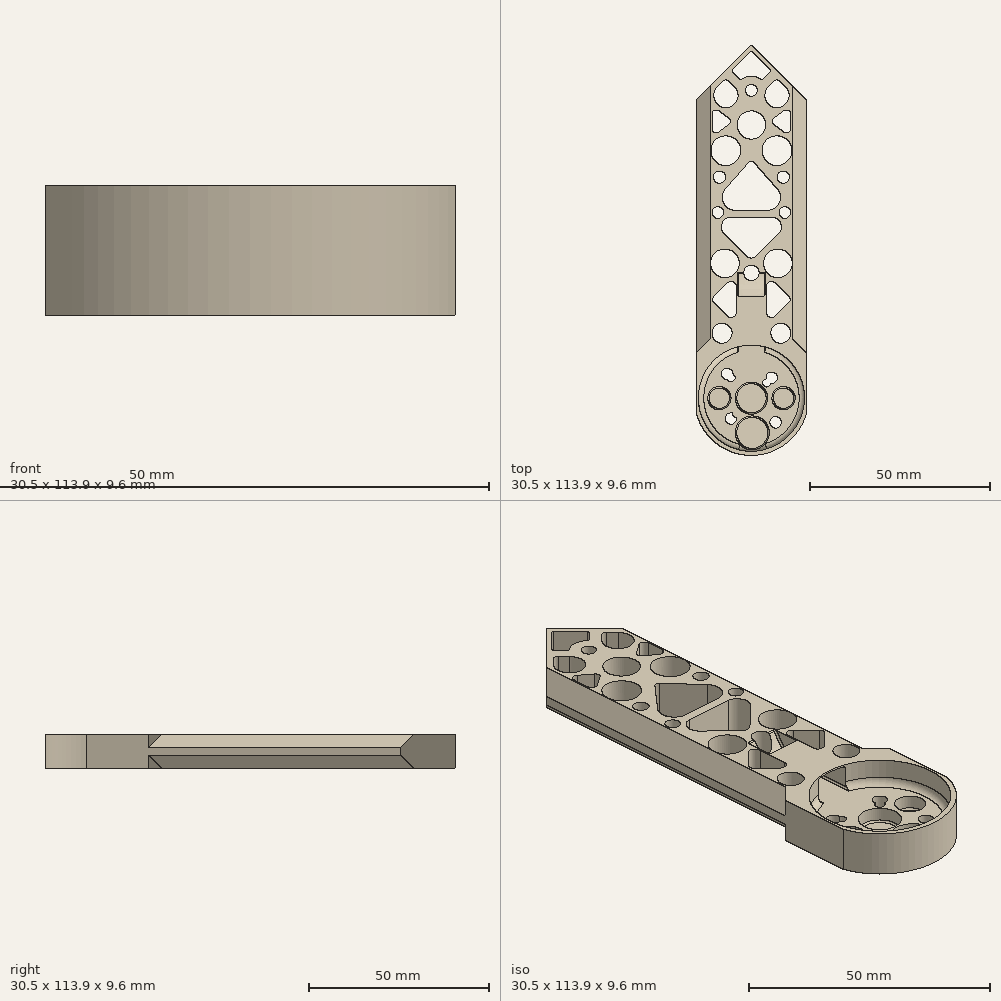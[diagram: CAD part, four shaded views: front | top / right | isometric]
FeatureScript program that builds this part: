
annotation { "Feature Type Name" : "Feature", "Feature Type Description" : "" }
export const myFeature = defineFeature(function(context is Context, id is Id, definition is map)
    precondition{}
    {
        {
            var Q0;
            Q0=qCreatedBy(makeId("Top.planeOp"),FACE);
            var sketch = newSketch(context, id + "F0", { "sketchPlane" : qUnion([Q0])});
            skLineSegment(sketch, "E0", {"start": v(0, 0) * mm, "end": v(-10, 0) * mm});
            skLineSegment(sketch, "E1", {"start": v(-7.84, 7.84) * mm, "end": v(0, 0) * mm});
            skLineSegment(sketch, "E2", {"start": v(-6.78, -6.78) * mm, "end": v(0, 0) * mm});
            skLineSegment(sketch, "E3", {"start": v(0, 0) * mm, "end": v(-5.66, -5.66) * mm});
            skCircle(sketch, "E4", {"center": v(-5.66, -5.66) * mm, "radius": 1.59 * mm});
            skLineSegment(sketch, "E5", {"start": v(0, 0) * mm, "end": v(-6.72, 6.72) * mm});
            skCircle(sketch, "E6", {"center": v(-6.72, 6.72) * mm, "radius": 1.59 * mm});
            skLineSegment(sketch, "E7", {"start": v(0, 0) * mm, "end": v(-5.66, 5.66) * mm});
            skCircle(sketch, "E8", {"center": v(-5.66, 5.66) * mm, "radius": 1.13 * mm});
            skLineSegment(sketch, "E9.MirrorCS", {"start": v(7.84, -7.84) * mm, "end": v(0, 0) * mm});
            skLineSegment(sketch, "E10.MirrorCS", {"start": v(0, 0) * mm, "end": v(5.66, -5.66) * mm});
            skCircle(sketch, "E11.MirrorC", {"center": v(6.72, -6.72) * mm, "radius": 1.59 * mm});
            skCircle(sketch, "E12.MirrorC", {"center": v(5.66, -5.66) * mm, "radius": 1.13 * mm});
            skLineSegment(sketch, "E13.MirrorCS", {"start": v(0, 0) * mm, "end": v(6.72, -6.72) * mm});
            skCircle(sketch, "E14.MirrorC", {"center": v(5.66, 5.66) * mm, "radius": 1.59 * mm});
            skLineSegment(sketch, "E15.MirrorCS", {"start": v(0, 0) * mm, "end": v(5.66, 5.66) * mm});
            skLineSegment(sketch, "E16.MirrorCS", {"start": v(6.78, 6.78) * mm, "end": v(0, 0) * mm});
            skPoint(sketch, "E17.MirrorCS.start.orphan", {"position": v(0, 10) * mm});
            skPoint(sketch, "E18.orphan", {"position": v(10, 10) * mm});
            skPoint(sketch, "E19.orphan", {"position": v(10, -10) * mm});
            skPoint(sketch, "E20.orphan", {"position": v(-10, 10) * mm});
            skPoint(sketch, "E21.orphan", {"position": v(-10, -10) * mm});
            skCircle(sketch, "E22", {"center": v(-4.24, -4.24) * mm, "radius": 1.13 * mm});
            skCircle(sketch, "E23", {"center": v(4.24, 4.24) * mm, "radius": 1.13 * mm});
            skSolve(sketch);
        }
        {
            var Q0;
            Q0=qCreatedBy(makeId("Front.planeOp"),FACE);
            var sketch = newSketch(context, id + "F1", { "sketchPlane" : qUnion([Q0])});
            skLineSegment(sketch, "E24", {"start": v(0, 0) * mm, "end": v(11.35, 0) * mm});
            skLineSegment(sketch, "E25", {"start": v(-11.35, 0) * mm, "end": v(0, 0) * mm});
            skLineSegment(sketch, "E26", {"start": v(0, 0) * mm, "end": v(0, 3.8) * mm});
            skLineSegment(sketch, "E27", {"start": v(0, 3.8) * mm, "end": v(15.25, 3.8) * mm});
            skLineSegment(sketch, "E28", {"start": v(-15.25, 3.8) * mm, "end": v(0, 3.8) * mm});
            skPoint(sketch, "E29.orphan", {"position": v(15.25, 0) * mm});
            skPoint(sketch, "E30.orphan", {"position": v(-15.25, 0) * mm});
            skLineSegment(sketch, "E31", {"start": v(-15.25, 3.8) * mm, "end": v(-11.35, 0) * mm});
            skLineSegment(sketch, "E32", {"start": v(15.25, 3.8) * mm, "end": v(11.35, 0) * mm});
            skLineSegment(sketch, "E33", {"start": v(15.25, 3.8) * mm, "end": v(15.25, 5.8) * mm});
            skLineSegment(sketch, "E34", {"start": v(15.25, 5.8) * mm, "end": v(11.35, 9.6) * mm});
            skLineSegment(sketch, "E35", {"start": v(11.35, 9.6) * mm, "end": v(0, 9.6) * mm});
            skLineSegment(sketch, "E36.MirrorCS", {"start": v(-11.35, 9.6) * mm, "end": v(0, 9.6) * mm});
            skLineSegment(sketch, "E37.MirrorCS", {"start": v(-15.25, 5.8) * mm, "end": v(-11.35, 9.6) * mm});
            skLineSegment(sketch, "E38.MirrorCS", {"start": v(-15.25, 3.8) * mm, "end": v(-15.25, 5.8) * mm});
            skSolve(sketch);
        }
        {
            var Q0;
            Q0=qSketchRegion(id+"F1",true);
            extrude(context, id + "F2", {"entities" : qUnion([Q0]), "depth" : 16.3 * mm, "hasSecondDirection" : true, "secondDirectionOppositeDirection" : true, "secondDirectionDepth" : 98 * mm});
        }
        {
            var Q0;
            Q0=qCreatedBy(makeId("Top.planeOp"),FACE);
            cPlane(context, id + "F3", {"entities" : qUnion([Q0]), "cplaneType" : CPlaneType.OFFSET, "offset" : 16 * mm, "width" : 150 * mm, "height" : 150 * mm});
        }
        {
            var Q0;
            Q0=makeQuery(id+"F2.opExtrude","SWEPT_FACE",FACE,{"disambiguationData":[OSD([sQuery(id+"F1.wireOp",EDGE,"E35"),sQuery(id+"F1.wireOp",EDGE,"E36.MirrorCS")])]});
            var sketch = newSketch(context, id + "F4", { "sketchPlane" : qUnion([Q0])});
            skCircle(sketch, "E39", {"center": v(0, 0) * mm, "radius": 14.75 * mm});
            skLineSegment(sketch, "E40", {"start": v(14.75, 0) * mm, "end": v(-14.75, 0) * mm});
            skSolve(sketch);
        }
        {
            var Q0;
            {var subQ0=sQuery(id+"F4.wireOp",EDGE,"E39");var subQ1=makeQuery(id+"F2.opExtrude","SWEPT_EDGE",EDGE,{"disambiguationData":[OSD([sQuery(id+"F1.wireOp",EDGE,"E34"),sQuery(id+"F1.wireOp",EDGE,"E35")])]});var subQ2=makeQuery(id+"F4.imprint","INTERSECT",VERTEX,{"disambiguationData":[OD(0.0)],"derivedFrom":[subQ1,subQ0]});Q0=makeQuery(id+"F4.imprint","IMPRINT",FACE,{"disambiguationData":[TD([[makeQuery(id+"F4.imprint","IMPRINT",EDGE,{"disambiguationData":[TD([[subQ2,-1.0]])],"derivedFrom":subQ0}),1.0]])]});}
            var Q1;
            {var subQ0=sQuery(id+"F4.wireOp",EDGE,"E39");var subQ1=makeQuery(id+"F2.opExtrude","SWEPT_EDGE",EDGE,{"disambiguationData":[OSD([sQuery(id+"F1.wireOp",EDGE,"E36.MirrorCS"),sQuery(id+"F1.wireOp",EDGE,"E37.MirrorCS")])]});var subQ2=makeQuery(id+"F4.imprint","INTERSECT",VERTEX,{"disambiguationData":[OD(1.0)],"derivedFrom":[subQ1,subQ0]});Q1=makeQuery(id+"F4.imprint","IMPRINT",FACE,{"disambiguationData":[TD([[makeQuery(id+"F4.imprint","IMPRINT",EDGE,{"disambiguationData":[TD([[subQ2,-1.0]])],"derivedFrom":subQ0}),1.0]])]});}
            var Q2;
            {var subQ0=sQuery(id+"F4.wireOp",EDGE,"E40");var subQ1=sQuery(id+"F4.wireOp",EDGE,"E39");var subQ2=makeQuery(id+"F4.imprint","INTERSECT",VERTEX,{"disambiguationData":[OD(1.0)],"derivedFrom":[subQ1,subQ0]});Q2=makeQuery(id+"F4.imprint","IMPRINT",FACE,{"disambiguationData":[TD([[makeQuery(id+"F4.imprint","IMPRINT",EDGE,{"disambiguationData":[TD([[subQ2,-1.0]])],"derivedFrom":subQ1}),1.0]])]});}
            var Q3;
            {var subQ0=sQuery(id+"F4.wireOp",EDGE,"E40");var subQ1=sQuery(id+"F4.wireOp",EDGE,"E39");var subQ2=makeQuery(id+"F4.imprint","INTERSECT",VERTEX,{"disambiguationData":[OD(1.0)],"derivedFrom":[subQ1,subQ0]});Q3=makeQuery(id+"F4.imprint","IMPRINT",FACE,{"disambiguationData":[TD([[makeQuery(id+"F4.imprint","IMPRINT",EDGE,{"disambiguationData":[TD([[subQ2,1.0]])],"derivedFrom":subQ1}),1.0]])]});}
            var Q4;
            {var subQ0=sQuery(id+"F4.wireOp",EDGE,"E40");var subQ1=sQuery(id+"F4.wireOp",EDGE,"E39");var subQ2=makeQuery(id+"F4.imprint","INTERSECT",VERTEX,{"disambiguationData":[OD(0.0)],"derivedFrom":[subQ1,subQ0]});Q4=makeQuery(id+"F4.imprint","IMPRINT",FACE,{"disambiguationData":[TD([[makeQuery(id+"F4.imprint","IMPRINT",EDGE,{"disambiguationData":[TD([[subQ2,-1.0]])],"derivedFrom":subQ1}),1.0]])]});}
            var Q5;
            {var subQ0=sQuery(id+"F4.wireOp",EDGE,"E40");var subQ1=sQuery(id+"F4.wireOp",EDGE,"E39");var subQ2=makeQuery(id+"F4.imprint","INTERSECT",VERTEX,{"disambiguationData":[OD(0.0)],"derivedFrom":[subQ1,subQ0]});Q5=makeQuery(id+"F4.imprint","IMPRINT",FACE,{"disambiguationData":[TD([[makeQuery(id+"F4.imprint","IMPRINT",EDGE,{"disambiguationData":[TD([[subQ2,1.0]])],"derivedFrom":subQ1}),1.0]])]});}
            extrude(context, id + "F5", {"entities" : qUnion([Q0, Q1, Q2, Q3, Q4, Q5]), "operationType" : NewBodyOperationType.REMOVE, "oppositeDirection" : true, "depth" : 5.6 * mm});
        }
        {
            var Q0;
            {var subQ5=sQuery(id+"F0.wireOp",EDGE,"E1");Q0=makeQuery(id+"F0.imprint","IMPRINT",FACE,{"disambiguationData":[TD([[makeQuery(id+"F0.imprint","IMPRINT",EDGE,{"derivedFrom":subQ5}),-1.0]])]});}
            var Q1;
            {var subQ3=sQuery(id+"F0.wireOp",EDGE,"E1");Q1=makeQuery(id+"F0.imprint","IMPRINT",FACE,{"disambiguationData":[TD([[makeQuery(id+"F0.imprint","IMPRINT",EDGE,{"derivedFrom":subQ3}),1.0]])]});}
            var Q2;
            {var subQ5=sQuery(id+"F0.wireOp",EDGE,"E2");Q2=makeQuery(id+"F0.imprint","IMPRINT",FACE,{"disambiguationData":[TD([[makeQuery(id+"F0.imprint","IMPRINT",EDGE,{"derivedFrom":subQ5}),1.0]])]});}
            var Q3;
            {var subQ5=sQuery(id+"F0.wireOp",EDGE,"E2");Q3=makeQuery(id+"F0.imprint","IMPRINT",FACE,{"disambiguationData":[TD([[makeQuery(id+"F0.imprint","IMPRINT",EDGE,{"derivedFrom":subQ5}),-1.0]])]});}
            var Q4;
            {var subQ0=sQuery(id+"F0.wireOp",EDGE,"E22");var subQ3=sQuery(id+"F0.wireOp",EDGE,"E3");var subQ4=makeQuery(id+"F0.imprint","INTERSECT",VERTEX,{"disambiguationData":[OD(0.0)],"derivedFrom":[subQ3,subQ0]});Q4=makeQuery(id+"F0.imprint","IMPRINT",FACE,{"disambiguationData":[TD([[makeQuery(id+"F0.imprint","IMPRINT",EDGE,{"disambiguationData":[TD([[subQ4,-1.0]])],"derivedFrom":subQ3}),1.0]])]});}
            var Q5;
            {var subQ0=sQuery(id+"F0.wireOp",EDGE,"E22");var subQ3=sQuery(id+"F0.wireOp",EDGE,"E3");var subQ4=makeQuery(id+"F0.imprint","INTERSECT",VERTEX,{"disambiguationData":[OD(0.0)],"derivedFrom":[subQ3,subQ0]});Q5=makeQuery(id+"F0.imprint","IMPRINT",FACE,{"disambiguationData":[TD([[makeQuery(id+"F0.imprint","IMPRINT",EDGE,{"disambiguationData":[TD([[subQ4,-1.0]])],"derivedFrom":subQ3}),-1.0]])]});}
            var Q6;
            {var subQ1=sQuery(id+"F0.wireOp",EDGE,"E6");var subQ3=sQuery(id+"F0.wireOp",EDGE,"E8");var subQ5=makeQuery(id+"F0.imprint","INTERSECT",VERTEX,{"disambiguationData":[OD(0.0)],"derivedFrom":[subQ1,subQ3]});Q6=makeQuery(id+"F0.imprint","IMPRINT",FACE,{"disambiguationData":[TD([[makeQuery(id+"F0.imprint","IMPRINT",EDGE,{"disambiguationData":[TD([[subQ5,-1.0]])],"derivedFrom":subQ1}),-1.0]])]});}
            var Q7;
            {var subQ1=sQuery(id+"F0.wireOp",EDGE,"E6");var subQ3=sQuery(id+"F0.wireOp",EDGE,"E8");var subQ5=makeQuery(id+"F0.imprint","INTERSECT",VERTEX,{"disambiguationData":[OD(1.0)],"derivedFrom":[subQ1,subQ3]});Q7=makeQuery(id+"F0.imprint","IMPRINT",FACE,{"disambiguationData":[TD([[makeQuery(id+"F0.imprint","IMPRINT",EDGE,{"disambiguationData":[TD([[subQ5,1.0]])],"derivedFrom":subQ1}),-1.0]])]});}
            var Q8;
            {var subQ3=sQuery(id+"F0.wireOp",EDGE,"E9.MirrorCS");Q8=makeQuery(id+"F0.imprint","IMPRINT",FACE,{"disambiguationData":[TD([[makeQuery(id+"F0.imprint","IMPRINT",EDGE,{"derivedFrom":subQ3}),1.0]])]});}
            var Q9;
            {var subQ3=sQuery(id+"F0.wireOp",EDGE,"E9.MirrorCS");Q9=makeQuery(id+"F0.imprint","IMPRINT",FACE,{"disambiguationData":[TD([[makeQuery(id+"F0.imprint","IMPRINT",EDGE,{"derivedFrom":subQ3}),-1.0]])]});}
            var Q10;
            {var subQ1=sQuery(id+"F0.wireOp",EDGE,"E11.MirrorC");var subQ3=sQuery(id+"F0.wireOp",EDGE,"E12.MirrorC");var subQ5=makeQuery(id+"F0.imprint","INTERSECT",VERTEX,{"disambiguationData":[OD(0.0)],"derivedFrom":[subQ1,subQ3]});Q10=makeQuery(id+"F0.imprint","IMPRINT",FACE,{"disambiguationData":[TD([[makeQuery(id+"F0.imprint","IMPRINT",EDGE,{"disambiguationData":[TD([[subQ5,-1.0]])],"derivedFrom":subQ1}),1.0]])]});}
            var Q11;
            {var subQ1=sQuery(id+"F0.wireOp",EDGE,"E11.MirrorC");var subQ3=sQuery(id+"F0.wireOp",EDGE,"E12.MirrorC");var subQ5=makeQuery(id+"F0.imprint","INTERSECT",VERTEX,{"disambiguationData":[OD(1.0)],"derivedFrom":[subQ1,subQ3]});Q11=makeQuery(id+"F0.imprint","IMPRINT",FACE,{"disambiguationData":[TD([[makeQuery(id+"F0.imprint","IMPRINT",EDGE,{"disambiguationData":[TD([[subQ5,1.0]])],"derivedFrom":subQ1}),1.0]])]});}
            var Q12;
            {var subQ0=sQuery(id+"F0.wireOp",EDGE,"E23");var subQ1=sQuery(id+"F0.wireOp",EDGE,"E14.MirrorC");var subQ2=makeQuery(id+"F0.imprint","INTERSECT",VERTEX,{"disambiguationData":[OD(1.0)],"derivedFrom":[subQ1,subQ0]});Q12=makeQuery(id+"F0.imprint","IMPRINT",FACE,{"disambiguationData":[TD([[makeQuery(id+"F0.imprint","IMPRINT",EDGE,{"disambiguationData":[TD([[subQ2,1.0]])],"derivedFrom":subQ1}),1.0]])]});}
            var Q13;
            {var subQ1=sQuery(id+"F0.wireOp",EDGE,"E16.MirrorCS");var subQ5=makeQuery(id+"F0.imprint","IMPRINT",VERTEX,{"derivedFrom":subQ1});Q13=makeQuery(id+"F0.imprint","IMPRINT",FACE,{"disambiguationData":[TD([[makeQuery(id+"F0.imprint","IMPRINT",EDGE,{"disambiguationData":[TD([[subQ5,1.0]])],"derivedFrom":subQ1}),-1.0]])]});}
            var Q14;
            {var subQ1=sQuery(id+"F0.wireOp",EDGE,"E16.MirrorCS");var subQ5=makeQuery(id+"F0.imprint","IMPRINT",VERTEX,{"derivedFrom":subQ1});Q14=makeQuery(id+"F0.imprint","IMPRINT",FACE,{"disambiguationData":[TD([[makeQuery(id+"F0.imprint","IMPRINT",EDGE,{"disambiguationData":[TD([[subQ5,1.0]])],"derivedFrom":subQ1}),1.0]])]});}
            var Q15;
            {var subQ1=sQuery(id+"F0.wireOp",EDGE,"E3");var subQ3=sQuery(id+"F0.wireOp",EDGE,"E4");var subQ5=makeQuery(id+"F0.imprint","INTERSECT",VERTEX,{"derivedFrom":[subQ1,subQ3]});Q15=makeQuery(id+"F0.imprint","IMPRINT",FACE,{"disambiguationData":[TD([[makeQuery(id+"F0.imprint","IMPRINT",EDGE,{"disambiguationData":[TD([[subQ5,-1.0]])],"derivedFrom":subQ1}),1.0]])]});}
            var Q16;
            {var subQ1=sQuery(id+"F0.wireOp",EDGE,"E3");var subQ3=sQuery(id+"F0.wireOp",EDGE,"E4");var subQ5=makeQuery(id+"F0.imprint","INTERSECT",VERTEX,{"derivedFrom":[subQ1,subQ3]});Q16=makeQuery(id+"F0.imprint","IMPRINT",FACE,{"disambiguationData":[TD([[makeQuery(id+"F0.imprint","IMPRINT",EDGE,{"disambiguationData":[TD([[subQ5,-1.0]])],"derivedFrom":subQ1}),-1.0]])]});}
            var Q17;
            {var subQ0=sQuery(id+"F0.wireOp",EDGE,"E13.MirrorCS");var subQ3=makeQuery(id+"F0.imprint","IMPRINT",VERTEX,{"derivedFrom":subQ0});Q17=makeQuery(id+"F0.imprint","IMPRINT",FACE,{"disambiguationData":[TD([[makeQuery(id+"F0.imprint","IMPRINT",EDGE,{"disambiguationData":[TD([[subQ3,1.0]])],"derivedFrom":subQ0}),1.0]])]});}
            var Q18;
            {var subQ0=sQuery(id+"F0.wireOp",EDGE,"E23");var subQ3=sQuery(id+"F0.wireOp",EDGE,"E14.MirrorC");var subQ4=makeQuery(id+"F0.imprint","INTERSECT",VERTEX,{"disambiguationData":[OD(1.0)],"derivedFrom":[subQ3,subQ0]});Q18=makeQuery(id+"F0.imprint","IMPRINT",FACE,{"disambiguationData":[TD([[makeQuery(id+"F0.imprint","IMPRINT",EDGE,{"disambiguationData":[TD([[subQ4,1.0]])],"derivedFrom":subQ3}),-1.0]])]});}
            var Q19;
            {var subQ0=sQuery(id+"F0.wireOp",EDGE,"E23");var subQ1=sQuery(id+"F0.wireOp",EDGE,"E14.MirrorC");var subQ2=makeQuery(id+"F0.imprint","INTERSECT",VERTEX,{"disambiguationData":[OD(0.0)],"derivedFrom":[subQ1,subQ0]});Q19=makeQuery(id+"F0.imprint","IMPRINT",FACE,{"disambiguationData":[TD([[makeQuery(id+"F0.imprint","IMPRINT",EDGE,{"disambiguationData":[TD([[subQ2,-1.0]])],"derivedFrom":subQ1}),1.0]])]});}
            var Q20;
            {var subQ0=sQuery(id+"F0.wireOp",EDGE,"E23");var subQ3=sQuery(id+"F0.wireOp",EDGE,"E14.MirrorC");var subQ4=makeQuery(id+"F0.imprint","INTERSECT",VERTEX,{"disambiguationData":[OD(0.0)],"derivedFrom":[subQ3,subQ0]});Q20=makeQuery(id+"F0.imprint","IMPRINT",FACE,{"disambiguationData":[TD([[makeQuery(id+"F0.imprint","IMPRINT",EDGE,{"disambiguationData":[TD([[subQ4,-1.0]])],"derivedFrom":subQ3}),-1.0]])]});}
            var Q21;
            {var subQ0=sQuery(id+"F0.wireOp",EDGE,"E13.MirrorCS");var subQ3=makeQuery(id+"F0.imprint","IMPRINT",VERTEX,{"derivedFrom":subQ0});Q21=makeQuery(id+"F0.imprint","IMPRINT",FACE,{"disambiguationData":[TD([[makeQuery(id+"F0.imprint","IMPRINT",EDGE,{"disambiguationData":[TD([[subQ3,1.0]])],"derivedFrom":subQ0}),-1.0]])]});}
            var Q22;
            {var subQ1=sQuery(id+"F0.wireOp",EDGE,"E5");var subQ5=sQuery(id+"F0.wireOp",EDGE,"E7");var subQ7=makeQuery(id+"F0.imprint","INTERSECT",VERTEX,{"derivedFrom":[subQ1,subQ5]});Q22=makeQuery(id+"F0.imprint","IMPRINT",FACE,{"disambiguationData":[TD([[makeQuery(id+"F0.imprint","IMPRINT",EDGE,{"disambiguationData":[TD([[subQ7,-1.0]])],"derivedFrom":subQ1}),1.0]])]});}
            var Q23;
            {var subQ1=sQuery(id+"F0.wireOp",EDGE,"E5");var subQ5=sQuery(id+"F0.wireOp",EDGE,"E7");var subQ7=makeQuery(id+"F0.imprint","INTERSECT",VERTEX,{"derivedFrom":[subQ1,subQ5]});Q23=makeQuery(id+"F0.imprint","IMPRINT",FACE,{"disambiguationData":[TD([[makeQuery(id+"F0.imprint","IMPRINT",EDGE,{"disambiguationData":[TD([[subQ7,-1.0]])],"derivedFrom":subQ1}),-1.0]])]});}
            extrude(context, id + "F6", {"entities" : qUnion([Q0, Q1, Q2, Q3, Q4, Q5, Q6, Q7, Q8, Q9, Q10, Q11, Q12, Q13, Q14, Q15, Q16, Q17, Q18, Q19, Q20, Q21, Q22, Q23]), "operationType" : NewBodyOperationType.REMOVE, "endBound" : BoundingType.THROUGH_ALL, "depth" : 5 * mm});
        }
        {
            var Q0;
            Q0=qCreatedBy(makeId("Top.planeOp"),FACE);
            var sketch = newSketch(context, id + "F7", { "sketchPlane" : qUnion([Q0])});
            skCircle(sketch, "E41", {"center": v(0, 0) * mm, "radius": 14.75 * mm});
            skArc(sketch, "E42", {"start": v(15.25, 4.5) * mm, "mid": v(0, 15.9) * mm, "end": v(-15.25, 4.5) * mm});
            skLineSegment(sketch, "E43", {"start": v(0, 0) * mm, "end": v(15.25, 0) * mm});
            skLineSegment(sketch, "E44", {"start": v(15.25, 0) * mm, "end": v(15.25, 4.5) * mm});
            skLineSegment(sketch, "E45.MirrorCS", {"start": v(15.25, 0) * mm, "end": v(15.25, -4.5) * mm});
            skLineSegment(sketch, "E46.MirrorCS", {"start": v(-15.25, 0) * mm, "end": v(-15.25, 4.5) * mm});
            skLineSegment(sketch, "E47.MirrorCS", {"start": v(-15.25, 0) * mm, "end": v(-15.25, -4.5) * mm});
            skArc(sketch, "E48.trimOffspring", {"start": v(-15.25, -4.5) * mm, "mid": v(0, -15.9) * mm, "end": v(15.25, -4.5) * mm});
            skSolve(sketch);
        }
        {
            var Q0;
            Q0=qSketchRegion(id+"F7",true);
            var Q1;
            Q1=makeQuery(id+"F2.opExtrude","SWEPT_FACE",FACE,{"disambiguationData":[OSD([sQuery(id+"F1.wireOp",EDGE,"E35"),sQuery(id+"F1.wireOp",EDGE,"E36.MirrorCS")])]});
            extrude(context, id + "F8", {"entities" : qUnion([Q0]), "operationType" : NewBodyOperationType.ADD, "endBound" : BoundingType.UP_TO_SURFACE, "endBoundEntityFace" : qUnion([Q1]), "depth" : 15.75 * mm});
        }
        {
            var Q0;
            Q0=qCreatedBy(id+"F3.planeOp",FACE);
            var sketch = newSketch(context, id + "F9", { "sketchPlane" : qUnion([Q0])});
            skCircle(sketch, "E49", {"center": v(0, 0) * mm, "radius": 15.9 * mm});
            skLineSegment(sketch, "E50", {"start": v(-15.9, 0) * mm, "end": v(-15.9, -16.3) * mm});
            skLineSegment(sketch, "E51.bottom", {"start": v(-15.9, -16.3) * mm, "end": v(15.9, -16.3) * mm});
            skLineSegment(sketch, "E51.top", {"start": v(-15.9, 0) * mm, "end": v(15.9, 0) * mm});
            skLineSegment(sketch, "E51.left", {"start": v(-15.9, -16.3) * mm, "end": v(-15.9, 0) * mm});
            skLineSegment(sketch, "E51.right", {"start": v(15.9, -16.3) * mm, "end": v(15.9, 0) * mm});
            skLineSegment(sketch, "E52", {"start": v(0, 0) * mm, "end": v(-3.75, 0) * mm});
            skLineSegment(sketch, "E53.bottom", {"start": v(-3.75, -16.3) * mm, "end": v(3.75, -16.3) * mm});
            skSolve(sketch);
        }
        {
            var Q0;
            {var subQ3=sQuery(id+"F9.wireOp",EDGE,"E51.left");Q0=makeQuery(id+"F9.imprint","IMPRINT",FACE,{"disambiguationData":[TD([[makeQuery(id+"F9.imprint","IMPRINT",EDGE,{"derivedFrom":subQ3}),-1.0]])]});}
            var Q1;
            {var subQ3=sQuery(id+"F9.wireOp",EDGE,"E51.left");Q1=makeQuery(id+"F9.imprint","IMPRINT",FACE,{"disambiguationData":[TD([[makeQuery(id+"F9.imprint","IMPRINT",EDGE,{"derivedFrom":subQ3}),-1.0]])]});}
            var Q2;
            {var subQ0=sQuery(id+"F9.wireOp",EDGE,"E51.right");Q2=makeQuery(id+"F9.imprint","IMPRINT",FACE,{"disambiguationData":[TD([[makeQuery(id+"F9.imprint","IMPRINT",EDGE,{"derivedFrom":subQ0}),1.0]])]});}
            extrude(context, id + "F10", {"entities" : qUnion([Q0, Q1, Q2]), "operationType" : NewBodyOperationType.REMOVE, "oppositeDirection" : true, "depth" : 25 * mm});
        }
        {
            var Q0;
            Q0=makeQuery(id+"F5.boolean.opBoolean","COPY",FACE,{"derivedFrom":makeQuery(id+"F5.opExtrude","CAP_FACE",FACE,{"disambiguationData":[OSD([sQuery(id+"F4.wireOp",EDGE,"E39")])],"isStart":false})});
            var sketch = newSketch(context, id + "F11", { "sketchPlane" : qUnion([Q0])});
            skCircle(sketch, "E54", {"center": v(0, 0) * mm, "radius": 4.47 * mm});
            skLineSegment(sketch, "E55", {"start": v(0, 0) * mm, "end": v(8.91, 0) * mm});
            skCircle(sketch, "E56", {"center": v(0.24, -9.63) * mm, "radius": 4.72 * mm});
            skLineSegment(sketch, "E57.MirrorCS", {"start": v(0, 0) * mm, "end": v(-8.91, 0) * mm});
            skCircle(sketch, "E58", {"center": v(8.91, 0) * mm, "radius": 3.24 * mm});
            skCircle(sketch, "E59.MirrorC", {"center": v(-8.91, 0) * mm, "radius": 3.24 * mm});
            skSolve(sketch);
        }
        {
            var Q0;
            Q0=qSketchRegion(id+"F11",true);
            extrude(context, id + "F12", {"entities" : qUnion([Q0]), "operationType" : NewBodyOperationType.REMOVE, "oppositeDirection" : true, "depth" : 3.2 * mm});
        }
        {
            var Q0;
            Q0=qCreatedBy(makeId("Top.planeOp"),FACE);
            cPlane(context, id + "F13", {"entities" : qUnion([Q0]), "cplaneType" : CPlaneType.OFFSET, "offset" : 0 * mm, "width" : 150 * mm, "height" : 150 * mm});
        }
        {
            var Q0;
            Q0=qCreatedBy(makeId("Top.planeOp"),FACE);
            var sketch = newSketch(context, id + "F14", { "sketchPlane" : qUnion([Q0])});
            skLineSegment(sketch, "E60", {"start": v(0, 82.75) * mm, "end": v(15.25, 82.75) * mm});
            skLineSegment(sketch, "E61", {"start": v(15.25, 82.75) * mm, "end": v(0, 98) * mm});
            skLineSegment(sketch, "E62.MirrorCS", {"start": v(-15.25, 82.75) * mm, "end": v(0, 98) * mm});
            skLineSegment(sketch, "E63.MirrorCS", {"start": v(0, 82.75) * mm, "end": v(-15.25, 82.75) * mm});
            skLineSegment(sketch, "E64", {"start": v(-15.25, 82.75) * mm, "end": v(-15.25, 98) * mm});
            skLineSegment(sketch, "E65", {"start": v(-15.25, 98) * mm, "end": v(15.25, 98) * mm});
            skLineSegment(sketch, "E66", {"start": v(15.25, 98) * mm, "end": v(15.25, 82.75) * mm});
            skSolve(sketch);
        }
        {
            var Q0;
            Q0=makeQuery(id+"F14.imprint","IMPRINT",FACE,{"disambiguationData":[TD([[makeQuery(id+"F14.imprint","IMPRINT",EDGE,{"derivedFrom":sQuery(id+"F14.wireOp",EDGE,"E61")}),-1.0]])]});
            var Q1;
            {var subQ0=sQuery(id+"F14.wireOp",EDGE,"E62.MirrorCS");Q1=makeQuery(id+"F14.imprint","IMPRINT",FACE,{"disambiguationData":[TD([[makeQuery(id+"F14.imprint","IMPRINT",EDGE,{"derivedFrom":subQ0}),1.0]])]});}
            extrude(context, id + "F15", {"entities" : qUnion([Q0, Q1]), "operationType" : NewBodyOperationType.REMOVE, "depth" : 25 * mm});
        }
        {
            var Q0;
            {var subQ0=sQuery(id+"F1.wireOp",EDGE,"E38.MirrorCS");var subQ1=sQuery(id+"F1.wireOp",EDGE,"E37.MirrorCS");var subQ2=sQuery(id+"F1.wireOp",EDGE,"E36.MirrorCS");var subQ3=sQuery(id+"F1.wireOp",EDGE,"E35");var subQ4=sQuery(id+"F1.wireOp",EDGE,"E34");var subQ5=sQuery(id+"F1.wireOp",EDGE,"E33");var subQ6=sQuery(id+"F1.wireOp",EDGE,"E32");var subQ7=sQuery(id+"F1.wireOp",EDGE,"E31");var subQ8=sQuery(id+"F1.wireOp",EDGE,"E25");var subQ9=sQuery(id+"F1.wireOp",EDGE,"E24");var subQ13=makeQuery(id+"F2.opExtrude","SWEPT_FACE",FACE,{"disambiguationData":[OSD([subQ3,subQ2])]});Q0=makeQuery(id+"F8.boolean.opBoolean","MERGE",FACE,{"derivedFrom":[makeQuery(id+"F5.boolean.opBoolean","SPLIT",FACE,{"disambiguationData":[TD([makeQuery(id+"F2.opExtrude","CAP_FACE",FACE,{"disambiguationData":[OSD([subQ9,subQ8,subQ7,subQ6,subQ5,subQ4,subQ3,subQ2,subQ1,subQ0])],"isStart":true})])],"derivedFrom":subQ13}),makeQuery(id+"F5.boolean.opBoolean","SPLIT",FACE,{"disambiguationData":[TD([makeQuery(id+"F2.opExtrude","CAP_FACE",FACE,{"disambiguationData":[OSD([subQ9,subQ8,subQ7,subQ6,subQ5,subQ4,subQ3,subQ2,subQ1,subQ0])],"isStart":false})])],"derivedFrom":subQ13}),makeQuery(id+"F8.opExtrude","CAP_FACE",FACE,{"disambiguationData":[OSD([sQuery(id+"F7.wireOp",EDGE,"E41"),sQuery(id+"F7.wireOp",EDGE,"E42")])],"isStart":false})]});}
            var sketch = newSketch(context, id + "F16", { "sketchPlane" : qUnion([Q0])});
            skLineSegment(sketch, "E67", {"start": v(0, 98) * mm, "end": v(0, 85.5) * mm});
            skCircle(sketch, "E68", {"center": v(0, 85.5) * mm, "radius": 1.6 * mm});
            skLineSegment(sketch, "E69.0", {"start": v(5.2, 91.2) * mm, "end": v(0.28, 96.12) * mm});
            skLineSegment(sketch, "E69.1", {"start": v(-5.23, 91.17) * mm, "end": v(-0.28, 96.12) * mm});
            skPoint(sketch, "E70.visualSharp", {"position": v(0, 96.4) * mm});
            skArc(sketch, "E70.filletArc", {"start": v(0.28, 96.12) * mm, "mid": v(0, 96.23) * mm, "end": v(-0.28, 96.12) * mm});
            skArc(sketch, "E71", {"start": v(2.58, 88.55) * mm, "mid": v(-0.02, 89.5) * mm, "end": v(-2.62, 88.52) * mm});
            skLineSegment(sketch, "E72.trimOffspring", {"start": v(-3.16, 88.54) * mm, "end": v(-5.23, 90.6) * mm});
            skLineSegment(sketch, "E73.trimOffspring", {"start": v(3.12, 88.58) * mm, "end": v(5.2, 90.64) * mm});
            skPoint(sketch, "E74.visualSharp", {"position": v(-5.51, 90.89) * mm});
            skArc(sketch, "E74.filletArc", {"start": v(-5.23, 91.17) * mm, "mid": v(-5.35, 90.89) * mm, "end": v(-5.23, 90.6) * mm});
            skPoint(sketch, "E75.visualSharp", {"position": v(5.47, 90.93) * mm});
            skArc(sketch, "E75.filletArc", {"start": v(5.2, 90.64) * mm, "mid": v(5.3, 90.93) * mm, "end": v(5.2, 91.2) * mm});
            skPoint(sketch, "E76.visualSharp", {"position": v(-2.89, 88.27) * mm});
            skArc(sketch, "E76.filletArc", {"start": v(-3.16, 88.54) * mm, "mid": v(-2.9, 88.43) * mm, "end": v(-2.62, 88.52) * mm});
            skPoint(sketch, "E77.visualSharp", {"position": v(2.85, 88.3) * mm});
            skArc(sketch, "E77.filletArc", {"start": v(2.58, 88.55) * mm, "mid": v(2.86, 88.46) * mm, "end": v(3.12, 88.58) * mm});
            skSolve(sketch);
        }
        {
            var Q0;
            {var subQ4=sQuery(id+"F16.wireOp",EDGE,"E69.0");Q0=makeQuery(id+"F16.imprint","IMPRINT",FACE,{"disambiguationData":[TD([[makeQuery(id+"F16.imprint","IMPRINT",EDGE,{"derivedFrom":subQ4}),1.0]])]});}
            var Q1;
            {var subQ4=sQuery(id+"F16.wireOp",EDGE,"E69.1");Q1=makeQuery(id+"F16.imprint","IMPRINT",FACE,{"disambiguationData":[TD([[makeQuery(id+"F16.imprint","IMPRINT",EDGE,{"derivedFrom":subQ4}),-1.0]])]});}
            var Q2;
            Q2=makeQuery(id+"F16.imprint","IMPRINT",FACE,{"disambiguationData":[TD([[makeQuery(id+"F16.imprint","IMPRINT",EDGE,{"derivedFrom":sQuery(id+"F16.wireOp",EDGE,"E68")}),1.0]])]});
            extrude(context, id + "F17", {"entities" : qUnion([Q0, Q1, Q2]), "operationType" : NewBodyOperationType.REMOVE, "oppositeDirection" : true, "depth" : 25 * mm});
        }
        {
            var Q0;
            Q0=qCreatedBy(makeId("Front.planeOp"),FACE);
            cPlane(context, id + "F18", {"entities" : qUnion([Q0]), "cplaneType" : CPlaneType.OFFSET, "offset" : 14 * mm, "oppositeDirection" : true, "width" : 150 * mm, "height" : 150 * mm});
        }
        {
            var Q0;
            Q0=qCreatedBy(id+"F18.planeOp",FACE);
            var sketch = newSketch(context, id + "F19", { "sketchPlane" : qUnion([Q0])});
            skLineSegment(sketch, "E78", {"start": v(4, 4) * mm, "end": v(4, 9.2) * mm});
            skLineSegment(sketch, "E79.bottom", {"start": v(3.6, 9.2) * mm, "end": v(-3.6, 9.2) * mm});
            skLineSegment(sketch, "E79.left", {"start": v(4, 8.8) * mm, "end": v(4, 4.4) * mm});
            skLineSegment(sketch, "E79.right", {"start": v(-4, 8.8) * mm, "end": v(-4, 4.4) * mm});
            skLineSegment(sketch, "E80", {"start": v(0, 0) * mm, "end": v(0, 4) * mm});
            skLineSegment(sketch, "E81", {"start": v(0, 4) * mm, "end": v(3.6, 4) * mm});
            skLineSegment(sketch, "E82", {"start": v(0, 4) * mm, "end": v(-3.6, 4) * mm});
            skPoint(sketch, "E83.orphan", {"position": v(-4, 0) * mm});
            skPoint(sketch, "E79.top.start.orphan", {"position": v(4, 0) * mm});
            skPoint(sketch, "E84.visualSharp", {"position": v(4, 4) * mm});
            skArc(sketch, "E84.filletArc", {"start": v(3.6, 4) * mm, "mid": v(3.88, 4.12) * mm, "end": v(4, 4.4) * mm});
            skPoint(sketch, "E85.visualSharp", {"position": v(-4, 4) * mm});
            skArc(sketch, "E85.filletArc", {"start": v(-4, 4.4) * mm, "mid": v(-3.88, 4.12) * mm, "end": v(-3.6, 4) * mm});
            skPoint(sketch, "E86.visualSharp", {"position": v(-4, 9.2) * mm});
            skArc(sketch, "E86.filletArc", {"start": v(-3.6, 9.2) * mm, "mid": v(-3.88, 9.08) * mm, "end": v(-4, 8.8) * mm});
            skPoint(sketch, "E87.visualSharp", {"position": v(4, 9.2) * mm});
            skArc(sketch, "E87.filletArc", {"start": v(4, 8.8) * mm, "mid": v(3.88, 9.08) * mm, "end": v(3.6, 9.2) * mm});
            skSolve(sketch);
        }
        {
            var Q0;
            Q0=qCreatedBy(makeId("Right.planeOp"),FACE);
            var sketch = newSketch(context, id + "F20", { "sketchPlane" : qUnion([Q0])});
            skLineSegment(sketch, "E88", {"start": v(0, 0) * mm, "end": v(14.4, 0) * mm});
            skLineSegment(sketch, "E89", {"start": v(14.4, 0) * mm, "end": v(14.4, 4) * mm});
            skLineSegment(sketch, "E90", {"start": v(14.4, 4) * mm, "end": v(26.4, 4) * mm});
            skLineSegment(sketch, "E91", {"start": v(26.4, 4) * mm, "end": v(35, 4) * mm});
            skLineSegment(sketch, "E92", {"start": v(35, 4) * mm, "end": v(35, 9.6) * mm});
            skFitSpline(sketch, "E93", {"points": [v(26.4, 4) * mm, v(30.4, 4.73) * mm, v(32.04, 5.93) * mm, v(33.82, 8.02) * mm, v(35, 9.6) * mm], "startDerivative": vector(21.55, 0) * mm, "endDerivative": vector(8.23, 6.38) * mm});
            skLineSegment(sketch, "E94", {"start": v(35, 9.6) * mm, "end": v(36.63, 9.93) * mm});
            skSolve(sketch);
        }
        {
            var Q0;
            Q0=makeQuery(id+"F19.imprint","IMPRINT",FACE,{"disambiguationData":[TD([[makeQuery(id+"F19.imprint","IMPRINT",EDGE,{"derivedFrom":sQuery(id+"F19.wireOp",EDGE,"E79.bottom")}),1.0]])]});
            var Q1;
            Q1=sQuery(id+"F20.wireOp",EDGE,"E93");
            var Q2;
            Q2=sQuery(id+"F20.wireOp",EDGE,"E90");
            var Q3;
            Q3=sQuery(id+"F20.wireOp",EDGE,"E94");
            sweep(context, id + "F21", {"operationType" : NewBodyOperationType.REMOVE, "profiles" : qUnion([Q0]), "path" : qUnion([Q1, Q2, Q3])});
        }
        {
            var Q0;
            Q0=qCreatedBy(id+"F13.planeOp",FACE);
            var sketch = newSketch(context, id + "F22", { "sketchPlane" : qUnion([Q0])});
            skLineSegment(sketch, "E95", {"start": v(0, 0) * mm, "end": v(0, 37.45) * mm});
            skLineSegment(sketch, "E96", {"start": v(-11.35, 37.45) * mm, "end": v(0, 37.45) * mm});
            skPoint(sketch, "E97.visualSharp", {"position": v(-11.35, 37.45) * mm});
            skLineSegment(sketch, "E98.MirrorCS", {"start": v(11.35, 37.45) * mm, "end": v(0, 37.45) * mm});
            skPoint(sketch, "E99.MirrorP", {"position": v(11.35, 37.45) * mm});
            skLineSegment(sketch, "E100", {"start": v(1.18, 39.4) * mm, "end": v(7.52, 45.52) * mm});
            skLineSegment(sketch, "E101", {"start": v(5.6, 50.25) * mm, "end": v(0, 50.25) * mm});
            skLineSegment(sketch, "E102", {"start": v(0, 50.25) * mm, "end": v(0, 52.25) * mm});
            skLineSegment(sketch, "E103", {"start": v(0, 52.25) * mm, "end": v(4.62, 52.25) * mm});
            skLineSegment(sketch, "E104", {"start": v(7.24, 58.07) * mm, "end": v(0.75, 65.4) * mm});
            skPoint(sketch, "E105.visualSharp", {"position": v(12.4, 52.25) * mm});
            skArc(sketch, "E105.filletArc", {"start": v(4.62, 52.25) * mm, "mid": v(7.82, 54.31) * mm, "end": v(7.24, 58.07) * mm});
            skPoint(sketch, "E106.visualSharp", {"position": v(12.4, 50.25) * mm});
            skArc(sketch, "E106.filletArc", {"start": v(7.52, 45.52) * mm, "mid": v(8.15, 48.53) * mm, "end": v(5.6, 50.25) * mm});
            skLineSegment(sketch, "E107.MirrorCS", {"start": v(-7.24, 58.07) * mm, "end": v(-0.75, 65.4) * mm});
            skLineSegment(sketch, "E108.MirrorCS", {"start": v(-5.6, 50.25) * mm, "end": v(0, 50.25) * mm});
            skLineSegment(sketch, "E109.MirrorCS", {"start": v(0, 52.25) * mm, "end": v(-4.62, 52.25) * mm});
            skArc(sketch, "E110.MirrorCS", {"start": v(-4.62, 52.25) * mm, "mid": v(-7.82, 54.31) * mm, "end": v(-7.24, 58.07) * mm});
            skArc(sketch, "E111.MirrorCS", {"start": v(-7.52, 45.52) * mm, "mid": v(-8.15, 48.53) * mm, "end": v(-5.6, 50.25) * mm});
            skLineSegment(sketch, "E112.MirrorCS", {"start": v(-1.18, 39.4) * mm, "end": v(-7.52, 45.52) * mm});
            skPoint(sketch, "E113.visualSharp", {"position": v(0, 66.25) * mm});
            skArc(sketch, "E113.filletArc", {"start": v(0.75, 65.4) * mm, "mid": v(0, 65.74) * mm, "end": v(-0.75, 65.4) * mm});
            skPoint(sketch, "E114.visualSharp", {"position": v(0, 38.25) * mm});
            skArc(sketch, "E114.filletArc", {"start": v(-1.18, 39.4) * mm, "mid": v(0, 38.92) * mm, "end": v(1.18, 39.4) * mm});
            skLineSegment(sketch, "E115", {"start": v(-11.2, 27.42) * mm, "end": v(-4.2, 27.42) * mm});
            skLineSegment(sketch, "E116", {"start": v(-4.2, 27.42) * mm, "end": v(-4.2, 31.04) * mm});
            skLineSegment(sketch, "E117", {"start": v(-6.59, 32.03) * mm, "end": v(-10.5, 28.13) * mm});
            skLineSegment(sketch, "E118.MirrorCS", {"start": v(-4.2, 27.42) * mm, "end": v(-4.2, 23.8) * mm});
            skLineSegment(sketch, "E119.MirrorCS", {"start": v(-6.59, 22.8) * mm, "end": v(-10.5, 26.71) * mm});
            skPoint(sketch, "E120.visualSharp", {"position": v(-4.2, 34.42) * mm});
            skArc(sketch, "E120.filletArc", {"start": v(-4.2, 31.04) * mm, "mid": v(-5.06, 32.33) * mm, "end": v(-6.59, 32.03) * mm});
            skPoint(sketch, "E121.visualSharp", {"position": v(-4.2, 20.42) * mm});
            skArc(sketch, "E121.filletArc", {"start": v(-6.59, 22.8) * mm, "mid": v(-5.06, 22.5) * mm, "end": v(-4.2, 23.8) * mm});
            skPoint(sketch, "E122.visualSharp", {"position": v(-11.2, 27.42) * mm});
            skArc(sketch, "E122.filletArc", {"start": v(-10.5, 28.13) * mm, "mid": v(-10.79, 27.42) * mm, "end": v(-10.5, 26.71) * mm});
            skLineSegment(sketch, "E123.MirrorCS", {"start": v(11.2, 27.42) * mm, "end": v(4.2, 27.42) * mm});
            skLineSegment(sketch, "E124.MirrorCS", {"start": v(6.59, 32.03) * mm, "end": v(10.5, 28.13) * mm});
            skArc(sketch, "E125.MirrorCS", {"start": v(10.5, 28.13) * mm, "mid": v(10.79, 27.42) * mm, "end": v(10.5, 26.71) * mm});
            skLineSegment(sketch, "E126.MirrorCS", {"start": v(4.2, 27.42) * mm, "end": v(4.2, 31.04) * mm});
            skArc(sketch, "E127.MirrorCS", {"start": v(4.2, 31.04) * mm, "mid": v(5.06, 32.33) * mm, "end": v(6.59, 32.03) * mm});
            skPoint(sketch, "E128.MirrorP", {"position": v(4.2, 20.42) * mm});
            skArc(sketch, "E129.MirrorCS", {"start": v(6.59, 22.8) * mm, "mid": v(5.06, 22.5) * mm, "end": v(4.2, 23.8) * mm});
            skLineSegment(sketch, "E130.MirrorCS", {"start": v(6.59, 22.8) * mm, "end": v(10.5, 26.71) * mm});
            skLineSegment(sketch, "E131.MirrorCS", {"start": v(4.2, 27.42) * mm, "end": v(4.2, 23.8) * mm});
            skPoint(sketch, "E132.MirrorP", {"position": v(11.2, 27.42) * mm});
            skCircle(sketch, "E133", {"center": v(7.36, 37.45) * mm, "radius": 4 * mm});
            skCircle(sketch, "E134.MirrorC", {"center": v(-7.36, 37.45) * mm, "radius": 4 * mm});
            skCircle(sketch, "E135", {"center": v(8.16, 18.04) * mm, "radius": 2.79 * mm});
            skCircle(sketch, "E136.MirrorC", {"center": v(-8.16, 18.04) * mm, "radius": 2.79 * mm});
            skCircle(sketch, "E137", {"center": v(7.1, 84.08) * mm, "radius": 3.38 * mm});
            skLineSegment(sketch, "E138", {"start": v(0, 80.7) * mm, "end": v(7.1, 80.7) * mm});
            skCircle(sketch, "E139.MirrorC", {"center": v(-7.1, 84.08) * mm, "radius": 3.38 * mm});
            skLineSegment(sketch, "E140", {"start": v(9.48, 86.46) * mm, "end": v(7.8, 88.14) * mm});
            skLineSegment(sketch, "E141", {"start": v(6.39, 88.14) * mm, "end": v(4.7, 86.46) * mm});
            skPoint(sketch, "E142.visualSharp", {"position": v(7.1, 88.85) * mm});
            skArc(sketch, "E142.filletArc", {"start": v(7.8, 88.14) * mm, "mid": v(7.1, 88.43) * mm, "end": v(6.39, 88.14) * mm});
            skLineSegment(sketch, "E143.MirrorCS", {"start": v(-6.39, 88.14) * mm, "end": v(-4.7, 86.46) * mm});
            skLineSegment(sketch, "E144.MirrorCS", {"start": v(-9.48, 86.46) * mm, "end": v(-7.8, 88.14) * mm});
            skArc(sketch, "E145.MirrorCS", {"start": v(-7.8, 88.14) * mm, "mid": v(-7.1, 88.43) * mm, "end": v(-6.39, 88.14) * mm});
            skCircle(sketch, "E146", {"center": v(0, 34.78) * mm, "radius": 2.14 * mm});
            skCircle(sketch, "E147", {"center": v(-7.1, 68.75) * mm, "radius": 4.15 * mm});
            skCircle(sketch, "E148.MirrorC", {"center": v(7.1, 68.75) * mm, "radius": 4.15 * mm});
            skCircle(sketch, "E149", {"center": v(0, 75.9) * mm, "radius": 3.93 * mm});
            skCircle(sketch, "E150", {"center": v(8.84, 61.4) * mm, "radius": 1.7 * mm});
            skCircle(sketch, "E151.MirrorC", {"center": v(-8.84, 61.4) * mm, "radius": 1.7 * mm});
            skCircle(sketch, "E152", {"center": v(9.32, 51.59) * mm, "radius": 1.63 * mm});
            skLineSegment(sketch, "E153", {"start": v(11.35, 37.45) * mm, "end": v(11.35, 86.98) * mm});
            skCircle(sketch, "E154.MirrorC", {"center": v(-9.32, 51.59) * mm, "radius": 1.63 * mm});
            skLineSegment(sketch, "E155", {"start": v(10.95, 76.9) * mm, "end": v(10.95, 74.93) * mm});
            skLineSegment(sketch, "E156", {"start": v(9.04, 73.96) * mm, "end": v(6.13, 76.09) * mm});
            skLineSegment(sketch, "E157", {"start": v(6.13, 77.7) * mm, "end": v(9.04, 79.83) * mm});
            skLineSegment(sketch, "E158", {"start": v(10.95, 78.86) * mm, "end": v(10.95, 76.9) * mm});
            skPoint(sketch, "E159.visualSharp", {"position": v(10.95, 72.56) * mm});
            skArc(sketch, "E159.filletArc", {"start": v(9.04, 73.96) * mm, "mid": v(10.3, 73.86) * mm, "end": v(10.95, 74.93) * mm});
            skPoint(sketch, "E160.visualSharp", {"position": v(10.95, 81.23) * mm});
            skArc(sketch, "E160.filletArc", {"start": v(10.95, 78.86) * mm, "mid": v(10.3, 79.93) * mm, "end": v(9.04, 79.83) * mm});
            skPoint(sketch, "E161.visualSharp", {"position": v(5.03, 76.9) * mm});
            skArc(sketch, "E161.filletArc", {"start": v(6.13, 77.7) * mm, "mid": v(5.73, 76.9) * mm, "end": v(6.13, 76.09) * mm});
            skArc(sketch, "E162.MirrorCS", {"start": v(-6.13, 77.7) * mm, "mid": v(-5.73, 76.9) * mm, "end": v(-6.13, 76.09) * mm});
            skLineSegment(sketch, "E163.MirrorCS", {"start": v(-10.95, 76.9) * mm, "end": v(-10.95, 74.93) * mm});
            skLineSegment(sketch, "E164.MirrorCS", {"start": v(-6.13, 77.7) * mm, "end": v(-9.04, 79.83) * mm});
            skLineSegment(sketch, "E165.MirrorCS", {"start": v(-9.04, 73.96) * mm, "end": v(-6.13, 76.09) * mm});
            skLineSegment(sketch, "E166.MirrorCS", {"start": v(-10.95, 78.86) * mm, "end": v(-10.95, 76.9) * mm});
            skLineSegment(sketch, "E167.MirrorCS", {"start": v(-11.35, 37.45) * mm, "end": v(-11.35, 86.98) * mm});
            skArc(sketch, "E168.MirrorCS", {"start": v(-9.04, 73.96) * mm, "mid": v(-10.3, 73.86) * mm, "end": v(-10.95, 74.93) * mm});
            skArc(sketch, "E169.MirrorCS", {"start": v(-10.95, 78.86) * mm, "mid": v(-10.3, 79.93) * mm, "end": v(-9.04, 79.83) * mm});
            skPoint(sketch, "E170.MirrorP", {"position": v(-5.03, 76.9) * mm});
            skSolve(sketch);
        }
        {
            var Q0;
            Q0=qSketchRegion(id+"F22",true);
            var Q1;
            {var subQ0=sQuery(id+"F1.wireOp",EDGE,"E37.MirrorCS");var subQ1=makeQuery(id+"F2.opExtrude","SWEPT_FACE",FACE,{"disambiguationData":[OSD([subQ0])]});var subQ2=sQuery(id+"F1.wireOp",EDGE,"E36.MirrorCS");var subQ3=sQuery(id+"F1.wireOp",EDGE,"E35");var subQ4=sQuery(id+"F1.wireOp",EDGE,"E38.MirrorCS");Q1=makeQuery(id+"F8.boolean.opBoolean","SPLIT",FACE,{"disambiguationData":[TD([makeQuery(id+"F2.opExtrude","CAP_FACE",FACE,{"disambiguationData":[OSD([sQuery(id+"F1.wireOp",EDGE,"E24"),sQuery(id+"F1.wireOp",EDGE,"E25"),sQuery(id+"F1.wireOp",EDGE,"E31"),sQuery(id+"F1.wireOp",EDGE,"E32"),sQuery(id+"F1.wireOp",EDGE,"E33"),sQuery(id+"F1.wireOp",EDGE,"E34"),subQ3,subQ2,subQ0,subQ4])],"isStart":true})])],"derivedFrom":subQ1});}
            extrude(context, id + "F23", {"entities" : qUnion([Q0]), "operationType" : NewBodyOperationType.REMOVE, "endBound" : BoundingType.UP_TO_SURFACE, "endBoundEntityFace" : qUnion([Q1]), "depth" : 8 * mm});
        }
        {
            var Q0;
            Q0=makeQuery(id+"F8.boolean.opBoolean","MERGE",FACE,{"derivedFrom":[makeQuery(id+"F2.opExtrude","SWEPT_FACE",FACE,{"disambiguationData":[OSD([sQuery(id+"F1.wireOp",EDGE,"E24"),sQuery(id+"F1.wireOp",EDGE,"E25")])]}),makeQuery(id+"F8.opExtrude","CAP_FACE",FACE,{"disambiguationData":[OSD([sQuery(id+"F7.wireOp",EDGE,"E41"),sQuery(id+"F7.wireOp",EDGE,"E42"),sQuery(id+"F7.wireOp",EDGE,"E44"),sQuery(id+"F7.wireOp",EDGE,"E45.MirrorCS"),sQuery(id+"F7.wireOp",EDGE,"E46.MirrorCS"),sQuery(id+"F7.wireOp",EDGE,"E47.MirrorCS"),sQuery(id+"F7.wireOp",EDGE,"E48.trimOffspring")])],"isStart":true})]});
            var sketch = newSketch(context, id + "F24", { "sketchPlane" : qUnion([Q0])});
            skLineSegment(sketch, "E171", {"start": v(11.35, -16.5) * mm, "end": v(11.35, -9.42) * mm});
            skLineSegment(sketch, "E172.MirrorCS", {"start": v(-11.35, -16.5) * mm, "end": v(-11.35, -9.42) * mm});
            skLineSegment(sketch, "E173", {"start": v(11.35, -16.5) * mm, "end": v(11.35, -12.6) * mm});
            skLineSegment(sketch, "E174", {"start": v(15.25, -4.5) * mm, "end": v(15.25, -12.6) * mm});
            skLineSegment(sketch, "E175.MirrorCS", {"start": v(-15.25, -4.5) * mm, "end": v(-15.25, -12.6) * mm});
            skLineSegment(sketch, "E176", {"start": v(11.35, -12.6) * mm, "end": v(11.35, -9.42) * mm});
            skLineSegment(sketch, "E177", {"start": v(11.35, -16.5) * mm, "end": v(15.25, -12.6) * mm});
            skLineSegment(sketch, "E178", {"start": v(-11.35, -16.5) * mm, "end": v(-15.25, -12.6) * mm});
            skLineSegment(sketch, "E179", {"start": v(11.35, -10.22) * mm, "end": v(15.25, -4.5) * mm});
            skLineSegment(sketch, "E180.MirrorCS", {"start": v(-11.35, -10.22) * mm, "end": v(-15.25, -4.5) * mm});
            skPoint(sketch, "E181.MirrorCS.end.orphan", {"position": v(-15.25, -4.5) * mm});
            skSolve(sketch);
        }
        {
            var Q0;
            Q0=qSketchRegion(id+"F24",true);
            var Q1;
            {var subQ0=sQuery(id+"F1.wireOp",EDGE,"E38.MirrorCS");var subQ1=sQuery(id+"F1.wireOp",EDGE,"E37.MirrorCS");var subQ2=sQuery(id+"F1.wireOp",EDGE,"E36.MirrorCS");var subQ3=sQuery(id+"F1.wireOp",EDGE,"E35");var subQ4=sQuery(id+"F1.wireOp",EDGE,"E34");var subQ5=sQuery(id+"F1.wireOp",EDGE,"E33");var subQ6=sQuery(id+"F1.wireOp",EDGE,"E32");var subQ7=sQuery(id+"F1.wireOp",EDGE,"E31");var subQ8=sQuery(id+"F1.wireOp",EDGE,"E25");var subQ9=sQuery(id+"F1.wireOp",EDGE,"E24");var subQ13=makeQuery(id+"F2.opExtrude","SWEPT_FACE",FACE,{"disambiguationData":[OSD([subQ3,subQ2])]});Q1=makeQuery(id+"F8.boolean.opBoolean","MERGE",FACE,{"derivedFrom":[makeQuery(id+"F5.boolean.opBoolean","SPLIT",FACE,{"disambiguationData":[TD([makeQuery(id+"F2.opExtrude","CAP_FACE",FACE,{"disambiguationData":[OSD([subQ9,subQ8,subQ7,subQ6,subQ5,subQ4,subQ3,subQ2,subQ1,subQ0])],"isStart":true})])],"derivedFrom":subQ13}),makeQuery(id+"F5.boolean.opBoolean","SPLIT",FACE,{"disambiguationData":[TD([makeQuery(id+"F2.opExtrude","CAP_FACE",FACE,{"disambiguationData":[OSD([subQ9,subQ8,subQ7,subQ6,subQ5,subQ4,subQ3,subQ2,subQ1,subQ0])],"isStart":false})])],"derivedFrom":subQ13}),makeQuery(id+"F8.opExtrude","CAP_FACE",FACE,{"disambiguationData":[OSD([sQuery(id+"F7.wireOp",EDGE,"E41"),sQuery(id+"F7.wireOp",EDGE,"E42"),sQuery(id+"F7.wireOp",EDGE,"E44"),sQuery(id+"F7.wireOp",EDGE,"E45.MirrorCS"),sQuery(id+"F7.wireOp",EDGE,"E46.MirrorCS"),sQuery(id+"F7.wireOp",EDGE,"E47.MirrorCS"),sQuery(id+"F7.wireOp",EDGE,"E48.trimOffspring")])],"isStart":false})]});}
            extrude(context, id + "F25", {"entities" : qUnion([Q0]), "operationType" : NewBodyOperationType.ADD, "endBound" : BoundingType.UP_TO_SURFACE, "oppositeDirection" : true, "endBoundEntityFace" : qUnion([Q1]), "depth" : 25 * mm});
        }
        {
            var Q0;
            Q0=makeQuery(id+"F5.boolean.opBoolean","COPY",EDGE,{"derivedFrom":makeQuery(id+"F5.opExtrude","CAP_EDGE",EDGE,{"disambiguationData":[OSD([sQuery(id+"F4.wireOp",EDGE,"E39")])],"isStart":false})});
            fillet(context, id + "F26", {"entities" : qUnion([Q0]), "radius" : 1.5 * mm, "tangentPropagation" : true, "allowEdgeOverflow" : false});
        }
        {
            var Q0;
            Q0=makeQuery(id+"F12.boolean.opBoolean","COPY",EDGE,{"derivedFrom":makeQuery(id+"F12.opExtrude","CAP_EDGE",EDGE,{"disambiguationData":[OSD([sQuery(id+"F11.wireOp",EDGE,"E59.MirrorC")])],"isStart":false})});
            var Q1;
            Q1=makeQuery(id+"F12.boolean.opBoolean","COPY",EDGE,{"derivedFrom":makeQuery(id+"F12.opExtrude","CAP_EDGE",EDGE,{"disambiguationData":[OSD([sQuery(id+"F11.wireOp",EDGE,"E54")])],"isStart":false})});
            var Q2;
            Q2=makeQuery(id+"F12.boolean.opBoolean","COPY",EDGE,{"derivedFrom":makeQuery(id+"F12.opExtrude","CAP_EDGE",EDGE,{"disambiguationData":[OSD([sQuery(id+"F11.wireOp",EDGE,"E58")])],"isStart":false})});
            var Q3;
            Q3=makeQuery(id+"F12.boolean.opBoolean","COPY",EDGE,{"derivedFrom":makeQuery(id+"F12.opExtrude","CAP_EDGE",EDGE,{"disambiguationData":[OSD([sQuery(id+"F11.wireOp",EDGE,"E56")])],"isStart":false})});
            fillet(context, id + "F27", {"entities" : qUnion([Q0, Q1, Q2, Q3]), "radius" : .4 * mm, "tangentPropagation" : true, "allowEdgeOverflow" : false});
        }
    });
